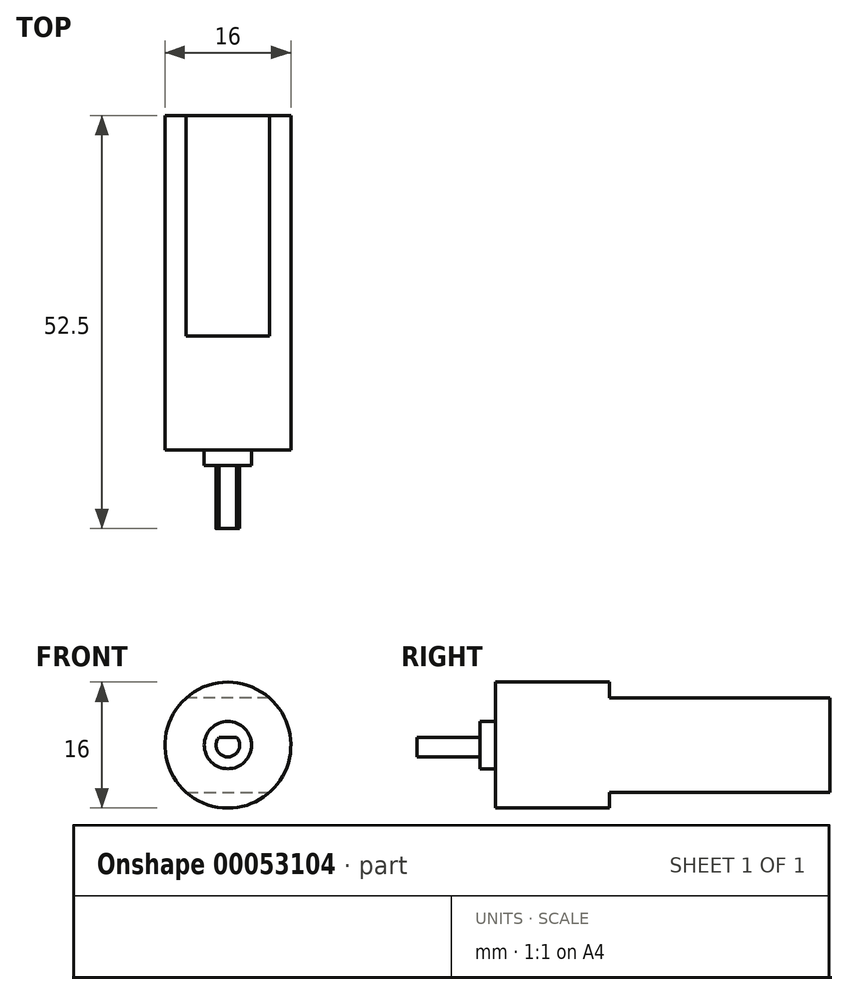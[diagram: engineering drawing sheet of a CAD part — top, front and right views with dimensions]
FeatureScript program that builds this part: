
annotation { "Feature Type Name" : "Feature", "Feature Type Description" : "" }
export const myFeature = defineFeature(function(context is Context, id is Id, definition is map)
    precondition{}
    {
        {
            var Q0;
            Q0=qCreatedBy(makeId("Front.planeOp"),FACE);
            var sketch = newSketch(context, id + "F0", { "sketchPlane" : qUnion([Q0])});
            skCircle(sketch, "E0", {"center": v(0, 0) * mm, "radius": 8 * mm});
            skCircle(sketch, "E1", {"center": v(-52.97, 46.26) * mm, "radius": 10 * mm});
            skSolve(sketch);
        }
        {
            var Q0;
            Q0=qSketchRegion(id+"F0",true);
            var Q1;
            Q1=makeQuery(id+"F0.imprint","IMPRINT",FACE,{"disambiguationData":[TD([[makeQuery(id+"F0.imprint","IMPRINT",EDGE,{"derivedFrom":sQuery(id+"F0.wireOp",EDGE,"E0")}),1.0]])]});
            extrude(context, id + "F1", {"entities" : qUnion([Q0, Q1]), "depth" : 14.5 * mm});
        }
        {
            var Q0;
            Q0=makeQuery(id+"F1.opExtrude","CAP_FACE",FACE,{"disambiguationData":[OSD([sQuery(id+"F0.wireOp",EDGE,"E0")])],"isStart":false});
            var sketch = newSketch(context, id + "F2", { "sketchPlane" : qUnion([Q0])});
            skCircle(sketch, "E2", {"center": v(0, 0) * mm, "radius": 3 * mm});
            skSolve(sketch);
        }
        {
            var Q0;
            Q0=qSketchRegion(id+"F2",true);
            var Q1;
            Q1=makeQuery(id+"F2.imprint","IMPRINT",FACE,{"disambiguationData":[TD([[makeQuery(id+"F2.imprint","IMPRINT",EDGE,{"derivedFrom":sQuery(id+"F2.wireOp",EDGE,"E2")}),1.0]])]});
            extrude(context, id + "F3", {"entities" : qUnion([Q0, Q1]), "operationType" : NewBodyOperationType.ADD, "depth" : 2 * mm});
        }
        {
            var Q0;
            Q0=makeQuery(id+"F3.opExtrude","CAP_FACE",FACE,{"disambiguationData":[OSD([sQuery(id+"F2.wireOp",EDGE,"E2")])],"isStart":false});
            var sketch = newSketch(context, id + "F4", { "sketchPlane" : qUnion([Q0])});
            skCircle(sketch, "E3", {"center": v(0, 0) * mm, "radius": 1.5 * mm});
            skLineSegment(sketch, "E4", {"start": v(0, 1) * mm, "end": v(0.47, 1) * mm});
            skLineSegment(sketch, "E5", {"start": v(0.47, 1) * mm, "end": v(-1.12, 1) * mm});
            skLineSegment(sketch, "E6", {"start": v(-1.12, 1) * mm, "end": v(1.12, 1) * mm});
            skSolve(sketch);
        }
        {
            var Q0;
            {var subQ0=sQuery(id+"F4.wireOp",EDGE,"E6");var subQ4=makeQuery(id+"F4.imprint","IMPRINT",VERTEX,{"disambiguationData":[OD(0.0)],"derivedFrom":subQ0});Q0=makeQuery(id+"F4.imprint","IMPRINT",FACE,{"disambiguationData":[TD([[makeQuery(id+"F4.imprint","IMPRINT",EDGE,{"disambiguationData":[TD([[subQ4,-1.0]])],"derivedFrom":subQ0}),-1.0]])]});}
            extrude(context, id + "F5", {"entities" : qUnion([Q0]), "operationType" : NewBodyOperationType.ADD, "depth" : 8 * mm});
        }
        {
            var Q0;
            Q0=makeQuery(id+"F1.opExtrude","CAP_FACE",FACE,{"disambiguationData":[OSD([sQuery(id+"F0.wireOp",EDGE,"E0")])],"isStart":true});
            var sketch = newSketch(context, id + "F6", { "sketchPlane" : qUnion([Q0])});
            skLineSegment(sketch, "E7", {"start": v(0, 6) * mm, "end": v(-5.3, 6) * mm});
            skLineSegment(sketch, "E8", {"start": v(0, 6) * mm, "end": v(5.3, 6) * mm});
            skLineSegment(sketch, "E9", {"start": v(0, -6) * mm, "end": v(-5.3, -6) * mm});
            skLineSegment(sketch, "E10", {"start": v(0, -6) * mm, "end": v(5.3, -6) * mm});
            skSolve(sketch);
        }
        {
            var Q0;
            {var subQ4=sQuery(id+"F6.wireOp",EDGE,"E7");Q0=makeQuery(id+"F6.imprint","IMPRINT",FACE,{"disambiguationData":[TD([[makeQuery(id+"F6.imprint","IMPRINT",EDGE,{"derivedFrom":subQ4}),1.0]])]});}
            extrude(context, id + "F7", {"entities" : qUnion([Q0]), "operationType" : NewBodyOperationType.ADD, "depth" : 28 * mm});
        }
        {
            var Q0;
            Q0=makeQuery(id+"F1.opExtrude","SWEPT_BODY",BODY,{"disambiguationData":[OSD([sQuery(id+"F0.wireOp",EDGE,"E1")])]});
            deleteBodies(context, id + "F8", {"entities" : qUnion([Q0])});
        }
    });
